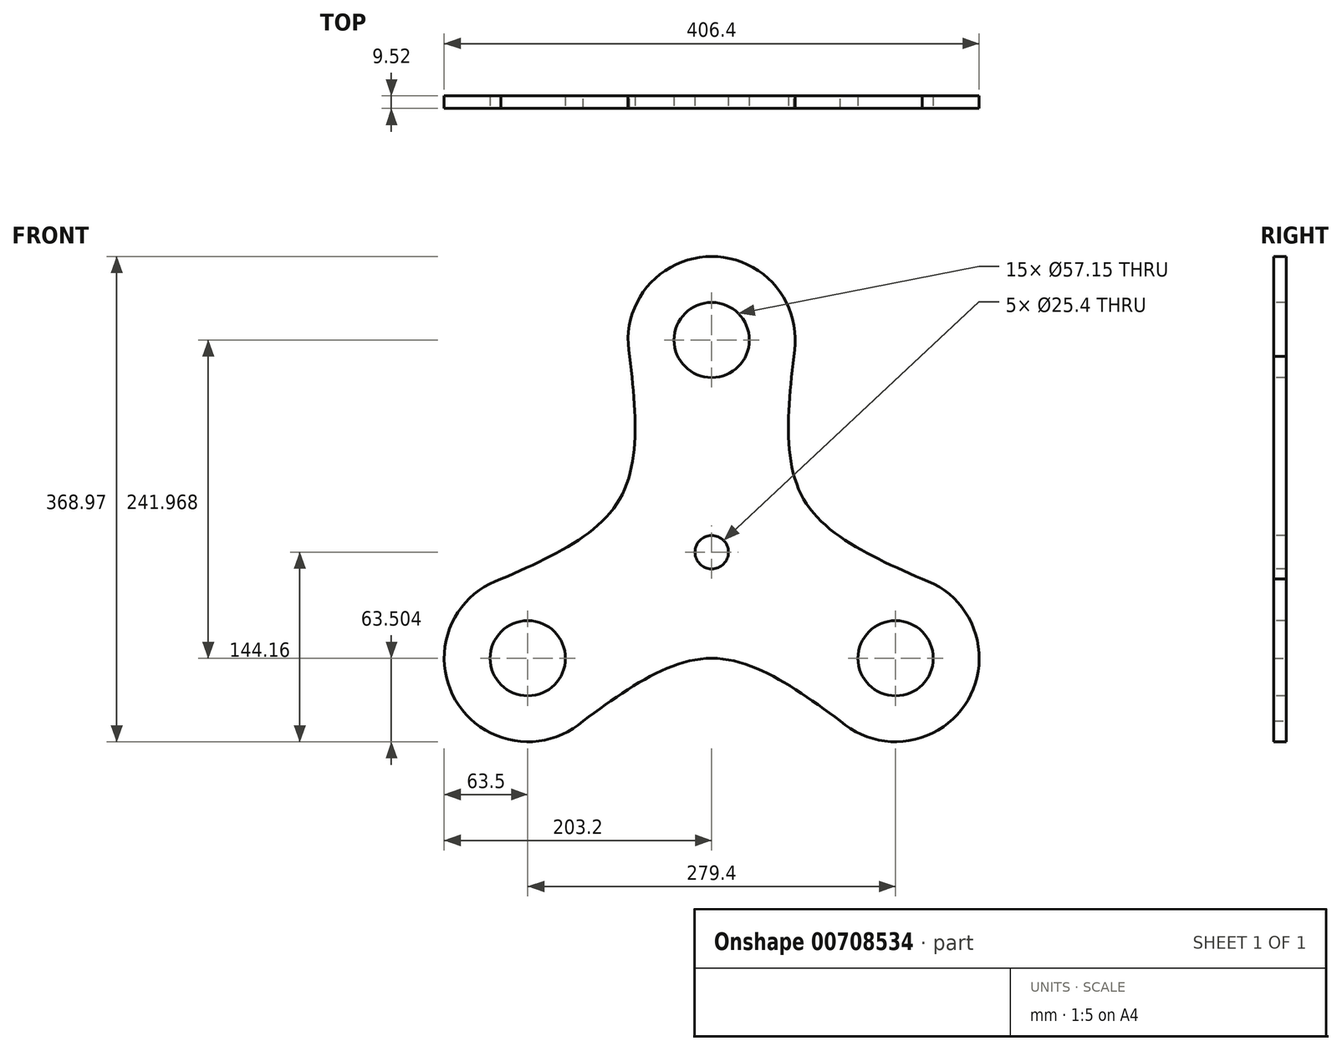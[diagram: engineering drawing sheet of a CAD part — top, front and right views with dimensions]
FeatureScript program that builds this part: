
annotation { "Feature Type Name" : "Feature", "Feature Type Description" : "" }
export const myFeature = defineFeature(function(context is Context, id is Id, definition is map)
    precondition{}
    {
        {
            var Q0;
            Q0=qCreatedBy(makeId("Front.planeOp"),FACE);
            var sketch = newSketch(context, id + "F0", { "sketchPlane" : qUnion([Q0])});
            skCircle(sketch, "E0.cCircle", {"center": v(0, 0) * mm, "radius": 161.31 * mm, "construction": true});
            skLineSegment(sketch, "E0.0", {"start": v(139.7, -80.66) * mm, "end": v(-139.7, -80.66) * mm});
            skLineSegment(sketch, "E0.1", {"start": v(-139.7, -80.66) * mm, "end": v(0, 161.31) * mm});
            skLineSegment(sketch, "E0.2", {"start": v(0, 161.31) * mm, "end": v(139.7, -80.66) * mm});
            skCircle(sketch, "E1", {"center": v(-139.7, -80.66) * mm, "radius": 63.5 * mm});
            skCircle(sketch, "E2", {"center": v(0, 161.31) * mm, "radius": 63.5 * mm});
            skCircle(sketch, "E3", {"center": v(139.7, -80.66) * mm, "radius": 63.5 * mm});
            skArc(sketch, "E4", {"start": v(-160.01, -20.5) * mm, "mid": v(-139.7, -80.66) * mm, "end": v(-97.75, -128.33) * mm});
            skFitSpline(sketch, "E5", {"points": [v(-160.01, -20.5) * mm, v(-69.85, 40.33) * mm, v(-62.26, 148.82) * mm], "startDerivative": vector(221.6, 97.8) * mm, "endDerivative": vector(-26.1, 240.82) * mm});
            skFitSpline(sketch, "E6", {"points": [v(-97.75, -128.33) * mm, v(0, -80.66) * mm, v(97.75, -128.33) * mm], "startDerivative": vector(195.5, 143.02) * mm, "endDerivative": vector(195.5, -143.02) * mm});
            skFitSpline(sketch, "E7", {"points": [v(62.26, 148.82) * mm, v(69.85, 40.33) * mm, v(160.01, -20.5) * mm], "startDerivative": vector(-26.1, -240.82) * mm, "endDerivative": vector(221.6, -97.8) * mm});
            skArc(sketch, "E8.trimOffspring", {"start": v(62.26, 148.82) * mm, "mid": v(0, 161.32) * mm, "end": v(-62.26, 148.82) * mm});
            skArc(sketch, "E9.trimOffspring", {"start": v(97.75, -128.33) * mm, "mid": v(139.7, -80.66) * mm, "end": v(160.01, -20.5) * mm});
            skSolve(sketch);
        }
        {
            var Q0;
            {var subQ0=sQuery(id+"F0.wireOp",EDGE,"E8.trimOffspring");Q0=makeQuery(id+"F0.imprint","IMPRINT",FACE,{"disambiguationData":[TD([[makeQuery(id+"F0.imprint","IMPRINT",EDGE,{"derivedFrom":subQ0}),-1.0]])]});}
            var Q1;
            {var subQ0=sQuery(id+"F0.wireOp",EDGE,"E8.trimOffspring");Q1=makeQuery(id+"F0.imprint","IMPRINT",FACE,{"disambiguationData":[TD([[makeQuery(id+"F0.imprint","IMPRINT",EDGE,{"derivedFrom":subQ0}),1.0]])]});}
            var Q2;
            {var subQ4=sQuery(id+"F0.wireOp",EDGE,"E0.0");var subQ5=makeQuery(id+"F0.imprint","INTERSECT",VERTEX,{"derivedFrom":[subQ4,sQuery(id+"F0.wireOp",EDGE,"E6")]});Q2=makeQuery(id+"F0.imprint","IMPRINT",FACE,{"disambiguationData":[TD([[makeQuery(id+"F0.imprint","IMPRINT",EDGE,{"disambiguationData":[TD([[subQ5,1.0]])],"derivedFrom":subQ4}),-1.0]])]});}
            var Q3;
            {var subQ0=sQuery(id+"F0.wireOp",EDGE,"E7");var subQ1=sQuery(id+"F0.wireOp",EDGE,"E0.2");var subQ2=makeQuery(id+"F0.imprint","INTERSECT",VERTEX,{"derivedFrom":[subQ1,subQ0]});Q3=makeQuery(id+"F0.imprint","IMPRINT",FACE,{"disambiguationData":[TD([[makeQuery(id+"F0.imprint","IMPRINT",EDGE,{"disambiguationData":[TD([[subQ2,1.0]])],"derivedFrom":subQ1}),1.0]])]});}
            var Q4;
            {var subQ0=sQuery(id+"F0.wireOp",EDGE,"E5");var subQ1=sQuery(id+"F0.wireOp",EDGE,"E0.1");var subQ2=makeQuery(id+"F0.imprint","INTERSECT",VERTEX,{"derivedFrom":[subQ1,subQ0]});Q4=makeQuery(id+"F0.imprint","IMPRINT",FACE,{"disambiguationData":[TD([[makeQuery(id+"F0.imprint","IMPRINT",EDGE,{"disambiguationData":[TD([[subQ2,-1.0]])],"derivedFrom":subQ1}),1.0]])]});}
            var Q5;
            {var subQ0=sQuery(id+"F0.wireOp",EDGE,"E0.2");var subQ1=sQuery(id+"F0.wireOp",EDGE,"E0.1");var subQ2=makeQuery(id+"F0.imprint","INTERSECT",VERTEX,{"derivedFrom":[subQ1,subQ0]});Q5=makeQuery(id+"F0.imprint","IMPRINT",FACE,{"disambiguationData":[TD([[makeQuery(id+"F0.imprint","IMPRINT",EDGE,{"disambiguationData":[TD([[subQ2,1.0]])],"derivedFrom":subQ1}),-1.0]])]});}
            var Q6;
            {var subQ0=sQuery(id+"F0.wireOp",EDGE,"E9.trimOffspring");Q6=makeQuery(id+"F0.imprint","IMPRINT",FACE,{"disambiguationData":[TD([[makeQuery(id+"F0.imprint","IMPRINT",EDGE,{"derivedFrom":subQ0}),-1.0]])]});}
            var Q7;
            {var subQ0=sQuery(id+"F0.wireOp",EDGE,"E0.2");var subQ1=sQuery(id+"F0.wireOp",EDGE,"E0.0");var subQ2=makeQuery(id+"F0.imprint","INTERSECT",VERTEX,{"derivedFrom":[subQ1,subQ0]});Q7=makeQuery(id+"F0.imprint","IMPRINT",FACE,{"disambiguationData":[TD([[makeQuery(id+"F0.imprint","IMPRINT",EDGE,{"disambiguationData":[TD([[subQ2,-1.0]])],"derivedFrom":subQ1}),-1.0]])]});}
            var Q8;
            {var subQ0=sQuery(id+"F0.wireOp",EDGE,"E9.trimOffspring");Q8=makeQuery(id+"F0.imprint","IMPRINT",FACE,{"disambiguationData":[TD([[makeQuery(id+"F0.imprint","IMPRINT",EDGE,{"derivedFrom":subQ0}),1.0]])]});}
            var Q9;
            {var subQ0=sQuery(id+"F0.wireOp",EDGE,"E7");var subQ1=sQuery(id+"F0.wireOp",EDGE,"E0.2");var subQ2=makeQuery(id+"F0.imprint","INTERSECT",VERTEX,{"derivedFrom":[subQ1,subQ0]});Q9=makeQuery(id+"F0.imprint","IMPRINT",FACE,{"disambiguationData":[TD([[makeQuery(id+"F0.imprint","IMPRINT",EDGE,{"disambiguationData":[TD([[subQ2,-1.0]])],"derivedFrom":subQ1}),1.0]])]});}
            var Q10;
            {var subQ0=sQuery(id+"F0.wireOp",EDGE,"E6");var subQ1=sQuery(id+"F0.wireOp",EDGE,"E0.0");var subQ2=makeQuery(id+"F0.imprint","INTERSECT",VERTEX,{"derivedFrom":[subQ1,subQ0]});Q10=makeQuery(id+"F0.imprint","IMPRINT",FACE,{"disambiguationData":[TD([[makeQuery(id+"F0.imprint","IMPRINT",EDGE,{"disambiguationData":[TD([[subQ2,1.0]])],"derivedFrom":subQ1}),1.0]])]});}
            var Q11;
            {var subQ0=sQuery(id+"F0.wireOp",EDGE,"E6");var subQ1=sQuery(id+"F0.wireOp",EDGE,"E0.0");var subQ2=makeQuery(id+"F0.imprint","INTERSECT",VERTEX,{"derivedFrom":[subQ1,subQ0]});Q11=makeQuery(id+"F0.imprint","IMPRINT",FACE,{"disambiguationData":[TD([[makeQuery(id+"F0.imprint","IMPRINT",EDGE,{"disambiguationData":[TD([[subQ2,-1.0]])],"derivedFrom":subQ1}),1.0]])]});}
            var Q12;
            {var subQ0=sQuery(id+"F0.wireOp",EDGE,"E4");Q12=makeQuery(id+"F0.imprint","IMPRINT",FACE,{"disambiguationData":[TD([[makeQuery(id+"F0.imprint","IMPRINT",EDGE,{"derivedFrom":subQ0}),1.0]])]});}
            var Q13;
            {var subQ0=sQuery(id+"F0.wireOp",EDGE,"E0.1");var subQ1=sQuery(id+"F0.wireOp",EDGE,"E0.0");var subQ2=makeQuery(id+"F0.imprint","INTERSECT",VERTEX,{"derivedFrom":[subQ1,subQ0]});Q13=makeQuery(id+"F0.imprint","IMPRINT",FACE,{"disambiguationData":[TD([[makeQuery(id+"F0.imprint","IMPRINT",EDGE,{"disambiguationData":[TD([[subQ2,1.0]])],"derivedFrom":subQ1}),-1.0]])]});}
            var Q14;
            {var subQ0=sQuery(id+"F0.wireOp",EDGE,"E4");Q14=makeQuery(id+"F0.imprint","IMPRINT",FACE,{"disambiguationData":[TD([[makeQuery(id+"F0.imprint","IMPRINT",EDGE,{"derivedFrom":subQ0}),-1.0]])]});}
            var Q15;
            {var subQ0=sQuery(id+"F0.wireOp",EDGE,"E5");var subQ1=sQuery(id+"F0.wireOp",EDGE,"E0.1");var subQ2=makeQuery(id+"F0.imprint","INTERSECT",VERTEX,{"derivedFrom":[subQ1,subQ0]});Q15=makeQuery(id+"F0.imprint","IMPRINT",FACE,{"disambiguationData":[TD([[makeQuery(id+"F0.imprint","IMPRINT",EDGE,{"disambiguationData":[TD([[subQ2,1.0]])],"derivedFrom":subQ1}),1.0]])]});}
            extrude(context, id + "F1", {"entities" : qUnion([Q0, Q1, Q2, Q3, Q4, Q5, Q6, Q7, Q8, Q9, Q10, Q11, Q12, Q13, Q14, Q15]), "endBound" : BoundingType.SYMMETRIC, "depth" : 9.52 * mm, "offsetDistance" : 25.4 * mm});
        }
        {
            var Q0;
            Q0=makeQuery(id+"F1.opExtrude","CAP_FACE",FACE,{"disambiguationData":[OSD([sQuery(id+"F0.wireOp",EDGE,"E1"),sQuery(id+"F0.wireOp",EDGE,"E2"),sQuery(id+"F0.wireOp",EDGE,"E3"),sQuery(id+"F0.wireOp",EDGE,"E5"),sQuery(id+"F0.wireOp",EDGE,"E6"),sQuery(id+"F0.wireOp",EDGE,"E7")])],"isStart":false});
            var sketch = newSketch(context, id + "F2", { "sketchPlane" : qUnion([Q0])});
            skPoint(sketch, "E10", {"position": v(-139.7, -80.66) * mm});
            skPoint(sketch, "E11", {"position": v(139.7, -80.66) * mm});
            skPoint(sketch, "E12", {"position": v(0, 161.31) * mm});
            skPoint(sketch, "E13", {"position": v(0, 0) * mm});
            skSolve(sketch);
        }
        {
            var Q0;
            Q0=sQuery(id+"F2.wireOp",VERTEX,"E10");
            var Q1;
            Q1=sQuery(id+"F2.wireOp",VERTEX,"E11");
            var Q2;
            Q2=sQuery(id+"F2.wireOp",VERTEX,"E12");
            var Q3;
            Q3=makeQuery(id+"F1.opExtrude","SWEPT_BODY",BODY,{"disambiguationData":[OSD([sQuery(id+"F0.wireOp",EDGE,"E1"),sQuery(id+"F0.wireOp",EDGE,"E2"),sQuery(id+"F0.wireOp",EDGE,"E3"),sQuery(id+"F0.wireOp",EDGE,"E5"),sQuery(id+"F0.wireOp",EDGE,"E6"),sQuery(id+"F0.wireOp",EDGE,"E7")])]});
            hole(context, id + "F3", {"style" : HoleStyle.SIMPLE, "endStyle" : HoleEndStyle.THROUGH, "holeDiameter" : 57.15 * mm, "majorDiameter" : 6.35 * mm, "isTappedThrough" : true, "tappedDepth" : 12.7 * mm, "tapClearance" : 3, "locations" : qUnion([Q0, Q1, Q2]), "scope" : qUnion([Q3])});
        }
        {
            var Q0;
            Q0=sQuery(id+"F2.wireOp",VERTEX,"E13");
            var Q1;
            Q1=makeQuery(id+"F1.opExtrude","SWEPT_BODY",BODY,{"disambiguationData":[OSD([sQuery(id+"F0.wireOp",EDGE,"E1"),sQuery(id+"F0.wireOp",EDGE,"E2"),sQuery(id+"F0.wireOp",EDGE,"E3"),sQuery(id+"F0.wireOp",EDGE,"E5"),sQuery(id+"F0.wireOp",EDGE,"E6"),sQuery(id+"F0.wireOp",EDGE,"E7")])]});
            hole(context, id + "F4", {"style" : HoleStyle.SIMPLE, "endStyle" : HoleEndStyle.THROUGH, "holeDiameter" : 25.4 * mm, "majorDiameter" : 6.35 * mm, "isTappedThrough" : true, "tappedDepth" : 12.7 * mm, "tapClearance" : 3, "locations" : qUnion([Q0]), "scope" : qUnion([Q1])});
        }
    });
